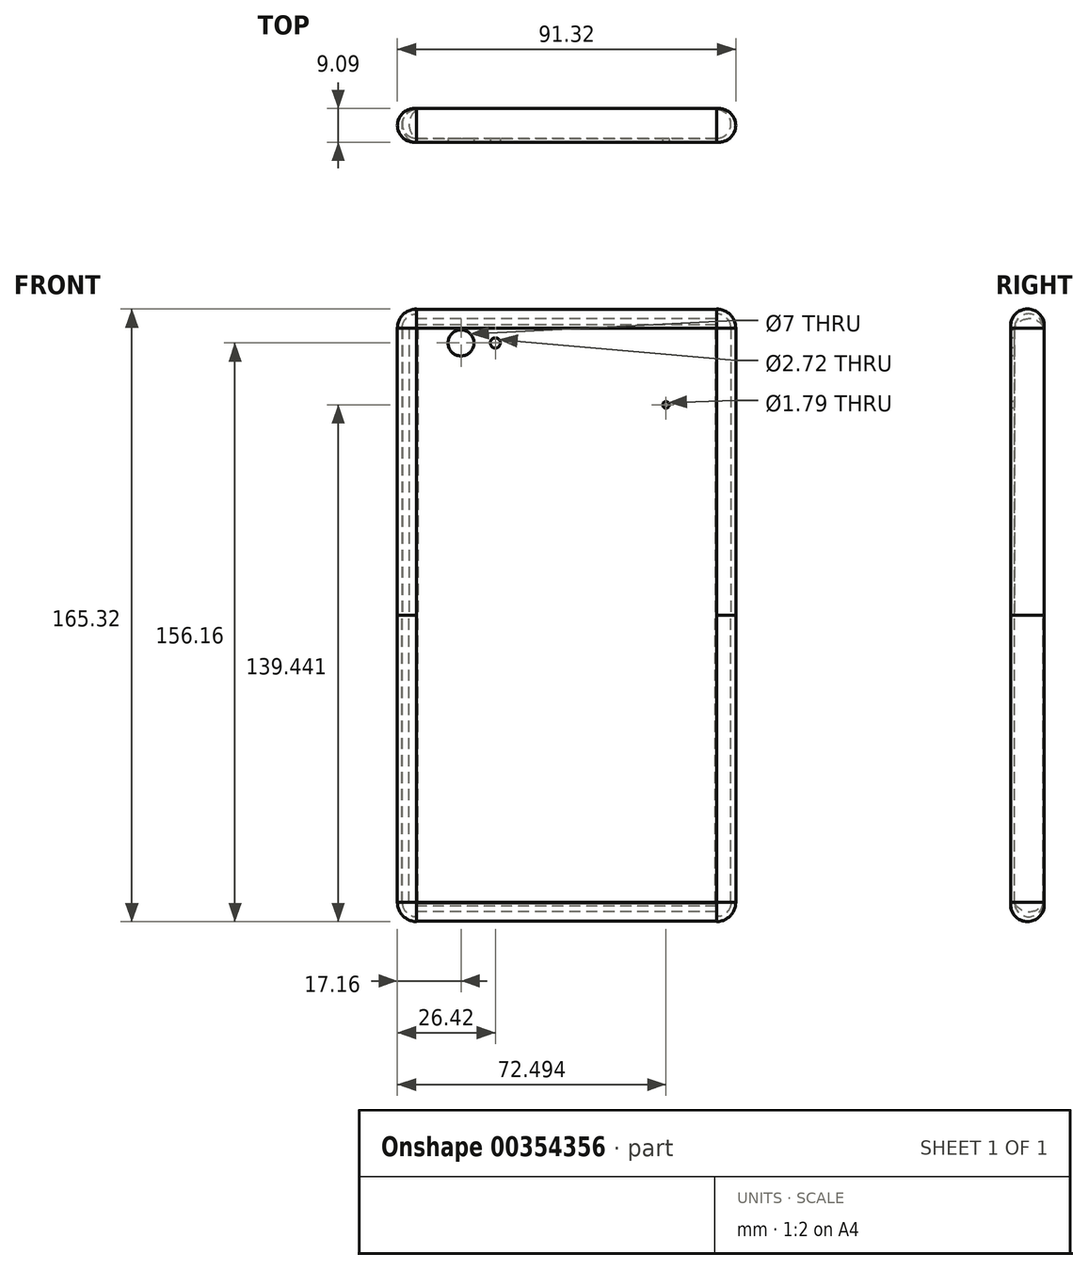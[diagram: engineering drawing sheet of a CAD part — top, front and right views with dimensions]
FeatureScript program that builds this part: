
annotation { "Feature Type Name" : "Feature", "Feature Type Description" : "" }
export const myFeature = defineFeature(function(context is Context, id is Id, definition is map)
    precondition{}
    {
        {
            var Q0;
            Q0=qCreatedBy(makeId("Front.planeOp"),FACE);
            var sketch = newSketch(context, id + "F0", { "sketchPlane" : qUnion([Q0])});
            skLineSegment(sketch, "E0.bottom", {"start": v(-40.5, 77.5) * mm, "end": v(40.5, 77.5) * mm});
            skLineSegment(sketch, "E0.top", {"start": v(-40.5, -77.5) * mm, "end": v(40.5, -77.5) * mm});
            skLineSegment(sketch, "E0.left", {"start": v(-40.5, 77.5) * mm, "end": v(-40.5, -77.5) * mm});
            skLineSegment(sketch, "E0.right", {"start": v(40.5, 77.5) * mm, "end": v(40.5, -77.5) * mm});
            skPoint(sketch, "E0.middle", {"position": v(0, 0) * mm});
            skCircle(sketch, "E1", {"center": v(-28.5, 73.5) * mm, "radius": 3.5 * mm});
            skCircle(sketch, "E2", {"center": v(-19.24, 73.5) * mm, "radius": 1.36 * mm});
            skCircle(sketch, "E3", {"center": v(26.83, 56.78) * mm, "radius": 0.9 * mm});
            skSolve(sketch);
        }
        {
            var Q0;
            Q0=qCreatedBy(makeId("Top.planeOp"),FACE);
            var sketch = newSketch(context, id + "F1", { "sketchPlane" : qUnion([Q0])});
            skArc(sketch, "E4", {"start": v(-40.51, 9.03) * mm, "mid": v(-44.51, 4.5) * mm, "end": v(-40.5, 0) * mm});
            skArc(sketch, "E5", {"start": v(40.5, 0) * mm, "mid": v(45.66, 4.5) * mm, "end": v(40.5, 9) * mm});
            skLineSegment(sketch, "E6", {"start": v(-40.5, 0) * mm, "end": v(-40.5, 1) * mm});
            skArc(sketch, "E7", {"start": v(-40.32, 8.7) * mm, "mid": v(-42.53, 4.9) * mm, "end": v(-40.5, 1) * mm});
            skLineSegment(sketch, "E8", {"start": v(-40.51, 9.03) * mm, "end": v(-40.32, 8.7) * mm});
            skLineSegment(sketch, "E9", {"start": v(40.5, 0) * mm, "end": v(40.5, 1) * mm});
            skArc(sketch, "E10", {"start": v(40.5, 1) * mm, "mid": v(44.36, 5.06) * mm, "end": v(40.1, 8.7) * mm});
            skLineSegment(sketch, "E11", {"start": v(40.1, 8.7) * mm, "end": v(40.5, 9) * mm});
            skSolve(sketch);
        }
        {
            var Q0;
            Q0 = qSketchRegion(id + "F0", true);
            extrude(context, id + "F2", {"entities" : qUnion([Q0]), "oppositeDirection" : true, "depth" : 1 * mm});
        }
        {
            var Q0;
            Q0=makeQuery(id+"F1.imprint","IMPRINT",FACE,{"disambiguationData":[TD([[makeQuery(id+"F1.imprint","IMPRINT",EDGE,{"derivedFrom":sQuery(id+"F1.wireOp",EDGE,"E5")}),1.0]])]});
            var Q1;
            Q1=makeQuery(id+"F1.imprint","IMPRINT",FACE,{"disambiguationData":[TD([[makeQuery(id+"F1.imprint","IMPRINT",EDGE,{"derivedFrom":sQuery(id+"F1.wireOp",EDGE,"E4")}),1.0]])]});
            extrude(context, id + "F3", {"entities" : qUnion([Q0, Q1]), "operationType" : NewBodyOperationType.ADD, "depth" : 77.5 * mm});
        }
        {
            var Q0;
            Q0=makeQuery(id+"F1.imprint","IMPRINT",FACE,{"disambiguationData":[TD([[makeQuery(id+"F1.imprint","IMPRINT",EDGE,{"derivedFrom":sQuery(id+"F1.wireOp",EDGE,"E5")}),1.0]])]});
            var Q1;
            Q1=makeQuery(id+"F1.imprint","IMPRINT",FACE,{"disambiguationData":[TD([[makeQuery(id+"F1.imprint","IMPRINT",EDGE,{"derivedFrom":sQuery(id+"F1.wireOp",EDGE,"E4")}),1.0]])]});
            extrude(context, id + "F4", {"entities" : qUnion([Q0, Q1]), "oppositeDirection" : true, "depth" : 77.5 * mm});
        }
        {
            var Q0;
            Q0=qCreatedBy(makeId("Right.planeOp"),FACE);
            var sketch = newSketch(context, id + "F5", { "sketchPlane" : qUnion([Q0])});
            skArc(sketch, "E12", {"start": v(9.05, 78.42) * mm, "mid": v(4.07, 82.57) * mm, "end": v(0, 77.53) * mm});
            skLineSegment(sketch, "E13", {"start": v(0, 0) * mm, "end": v(-9.51, 0) * mm});
            skLineSegment(sketch, "E14", {"start": v(0, 77.53) * mm, "end": v(0.97, 77.53) * mm});
            skArc(sketch, "E15", {"start": v(9.05, 77.5) * mm, "mid": v(5.02, 79.98) * mm, "end": v(0.97, 77.53) * mm});
            skLineSegment(sketch, "E16", {"start": v(9.05, 77.5) * mm, "end": v(9.05, 78.42) * mm});
            skSolve(sketch);
        }
        {
            var Q0;
            Q0=makeQuery(id+"F5.imprint","IMPRINT",FACE,{"disambiguationData":[TD([[makeQuery(id+"F5.imprint","IMPRINT",EDGE,{"derivedFrom":sQuery(id+"F5.wireOp",EDGE,"E12")}),1.0]])]});
            extrude(context, id + "F6", {"entities" : qUnion([Q0]), "depth" : 40.5 * mm});
        }
        {
            var Q0;
            Q0=makeQuery(id+"F6.opExtrude","CAP_FACE",FACE,{"disambiguationData":[OSD([sQuery(id+"F5.wireOp",EDGE,"E12"),sQuery(id+"F5.wireOp",EDGE,"E14"),sQuery(id+"F5.wireOp",EDGE,"E15"),sQuery(id+"F5.wireOp",EDGE,"E16")])],"isStart":true});
            extrude(context, id + "F7", {"entities" : qUnion([Q0]), "operationType" : NewBodyOperationType.ADD, "depth" : 40.5 * mm});
        }
        {
            var Q0;
            Q0=makeQuery(id+"F6.opExtrude","SWEPT_BODY",BODY,{"disambiguationData":[OSD([sQuery(id+"F5.wireOp",EDGE,"E12"),sQuery(id+"F5.wireOp",EDGE,"E14"),sQuery(id+"F5.wireOp",EDGE,"E15"),sQuery(id+"F5.wireOp",EDGE,"E16")])]});
            var Q1;
            Q1=qCreatedBy(makeId("Top.planeOp"),FACE);
            mirror(context, id + "F8", {"entities" : qUnion([Q0]), "mirrorPlane" : qUnion([Q1])});
        }
        {
            var Q0;
            Q0=makeQuery(id+"F3.opExtrude","CAP_FACE",FACE,{"disambiguationData":[OSD([sQuery(id+"F1.wireOp",EDGE,"E5"),sQuery(id+"F1.wireOp",EDGE,"E9"),sQuery(id+"F1.wireOp",EDGE,"E10"),sQuery(id+"F1.wireOp",EDGE,"E11")])],"isStart":false});
            var sketch = newSketch(context, id + "F9", { "sketchPlane" : qUnion([Q0])});
            skArc(sketch, "E17.0", {"start": v(40.5, 1) * mm, "mid": v(44.36, 5.06) * mm, "end": v(40.1, 8.7) * mm});
            skArc(sketch, "E17.1", {"start": v(40.5, 0) * mm, "mid": v(45.66, 4.5) * mm, "end": v(40.5, 9) * mm});
            skLineSegment(sketch, "E18", {"start": v(40.5, 9) * mm, "end": v(40.5, 8.72) * mm});
            skLineSegment(sketch, "E19", {"start": v(40.5, 8.72) * mm, "end": v(40.5, 1) * mm});
            skSolve(sketch);
        }
        {
            var Q0;
            Q0=makeQuery(id+"F9.imprint","IMPRINT",FACE,{"disambiguationData":[TD([[makeQuery(id+"F9.imprint","IMPRINT",EDGE,{"derivedFrom":sQuery(id+"F9.wireOp",EDGE,"E17.1")}),1.0]])]});
            var Q1;
            Q1=sQuery(id+"F9.wireOp",EDGE,"E19");
            revolve(context, id + "F10", {"entities" : qUnion([Q0]), "axis" : qUnion([Q1]), "revolveType" : RevolveType.ONE_DIRECTION, "angle" : 90 * degree});
        }
        {
            var Q0;
            Q0=makeQuery(id+"F10.opRevolve","SWEPT_BODY",BODY,{"disambiguationData":[OSD([sQuery(id+"F1.wireOp",EDGE,"E9"),sQuery(id+"F9.wireOp",EDGE,"E17.0"),sQuery(id+"F9.wireOp",EDGE,"E17.1"),sQuery(id+"F9.wireOp",EDGE,"E18")])]});
            var Q1;
            Q1=qCreatedBy(makeId("Top.planeOp"),FACE);
            mirror(context, id + "F11", {"entities" : qUnion([Q0]), "mirrorPlane" : qUnion([Q1])});
        }
        {
            var Q0;
            Q0=makeQuery(id+"F11.opPattern","COPY",BODY,{"derivedFrom":makeQuery(id+"F10.opRevolve","SWEPT_BODY",BODY,{"disambiguationData":[OSD([sQuery(id+"F1.wireOp",EDGE,"E9"),sQuery(id+"F9.wireOp",EDGE,"E17.0"),sQuery(id+"F9.wireOp",EDGE,"E17.1"),sQuery(id+"F9.wireOp",EDGE,"E18")])]}),"instanceName":"1"});
            var Q1;
            Q1=makeQuery(id+"F10.opRevolve","SWEPT_BODY",BODY,{"disambiguationData":[OSD([sQuery(id+"F1.wireOp",EDGE,"E9"),sQuery(id+"F9.wireOp",EDGE,"E17.0"),sQuery(id+"F9.wireOp",EDGE,"E17.1"),sQuery(id+"F9.wireOp",EDGE,"E18")])]});
            var Q2;
            Q2=qCreatedBy(makeId("Right.planeOp"),FACE);
            mirror(context, id + "F12", {"entities" : qUnion([Q0, Q1]), "mirrorPlane" : qUnion([Q2])});
        }
        {
            var Q0;
            Q0=makeQuery(id+"F4.opExtrude","SWEPT_BODY",BODY,{"disambiguationData":[OSD([sQuery(id+"F1.wireOp",EDGE,"E5"),sQuery(id+"F1.wireOp",EDGE,"E9"),sQuery(id+"F1.wireOp",EDGE,"E10"),sQuery(id+"F1.wireOp",EDGE,"E11")])]});
            var Q1;
            Q1=makeQuery(id+"F3.opExtrude","SWEPT_BODY",BODY,{"disambiguationData":[OSD([sQuery(id+"F1.wireOp",EDGE,"E5"),sQuery(id+"F1.wireOp",EDGE,"E9"),sQuery(id+"F1.wireOp",EDGE,"E10"),sQuery(id+"F1.wireOp",EDGE,"E11")])]});
            var Q2;
            Q2=qCreatedBy(makeId("Right.planeOp"),FACE);
            mirror(context, id + "F13", {"entities" : qUnion([Q0, Q1]), "mirrorPlane" : qUnion([Q2])});
        }
    });
